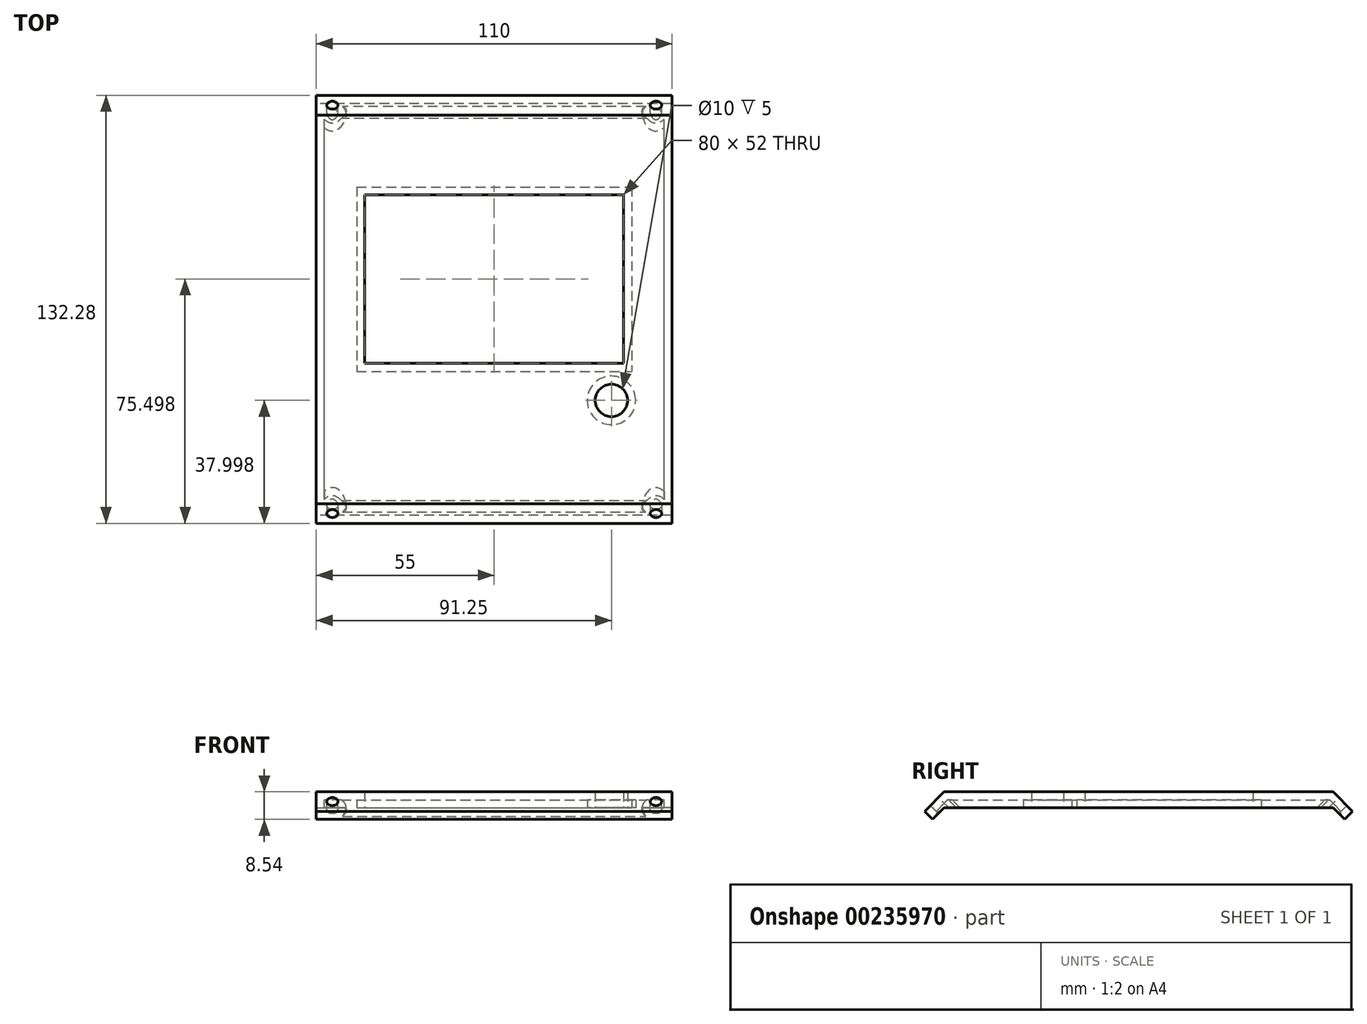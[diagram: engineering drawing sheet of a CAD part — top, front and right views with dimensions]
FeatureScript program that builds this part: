
annotation { "Feature Type Name" : "Feature", "Feature Type Description" : "" }
export const myFeature = defineFeature(function(context is Context, id is Id, definition is map)
    precondition{}
    {
        {
            var Q0;
            Q0=qCreatedBy(makeId("Top.planeOp"),FACE);
            var sketch = newSketch(context, id + "F0", { "sketchPlane" : qUnion([Q0])});
            skLineSegment(sketch, "E0", {"start": v(0, 0) * mm, "end": v(0, 120.2) * mm});
            skLineSegment(sketch, "E1.0", {"start": v(110, 0) * mm, "end": v(110, 120.2) * mm});
            skLineSegment(sketch, "E2", {"start": v(110, 120.2) * mm, "end": v(0, 120.2) * mm});
            skLineSegment(sketch, "E3", {"start": v(0, 0) * mm, "end": v(110, 0) * mm});
            skLineSegment(sketch, "E4.0", {"start": v(15, 95.46) * mm, "end": v(95, 95.46) * mm});
            skLineSegment(sketch, "E5.0", {"start": v(15, 95.46) * mm, "end": v(15, 43.46) * mm});
            skLineSegment(sketch, "E6.0", {"start": v(15, 43.46) * mm, "end": v(95, 43.46) * mm});
            skLineSegment(sketch, "E7.0", {"start": v(95, 95.46) * mm, "end": v(95, 43.46) * mm});
            skCircle(sketch, "E8.0", {"center": v(91.25, 31.96) * mm, "radius": 5 * mm});
            skSolve(sketch);
        }
        {
            var Q0;
            Q0 = qSketchRegion(id + "F0", true);
            extrude(context, id + "F1", {"entities" : qUnion([Q0]), "depth" : 5 * mm});
        }
        {
            var Q0;
            Q0=makeQuery(id+"F1.opExtrude","SWEPT_FACE",FACE,{"disambiguationData":[OSD([sQuery(id+"F0.wireOp",EDGE,"E0")])]});
            var sketch = newSketch(context, id + "F2", { "sketchPlane" : qUnion([Q0])});
            skLineSegment(sketch, "E9", {"start": v(0, 0) * mm, "end": v(3.54, -3.54) * mm});
            skLineSegment(sketch, "E10", {"start": v(3.54, -3.54) * mm, "end": v(6.04, -1.04) * mm});
            skLineSegment(sketch, "E11", {"start": v(6.04, -1.04) * mm, "end": v(0, 5) * mm});
            skLineSegment(sketch, "E12", {"start": v(-120.2, 0) * mm, "end": v(-123.74, -3.54) * mm});
            skLineSegment(sketch, "E13", {"start": v(-123.74, -3.54) * mm, "end": v(-126.24, -1.04) * mm});
            skLineSegment(sketch, "E14", {"start": v(-126.24, -1.04) * mm, "end": v(-120.2, 5) * mm});
            skLineSegment(sketch, "E15", {"start": v(-120.2, 0) * mm, "end": v(-120.2, 5) * mm});
            skLineSegment(sketch, "E16", {"start": v(0, 0) * mm, "end": v(0, 5) * mm});
            skSolve(sketch);
        }
        {
            var Q0;
            Q0 = qSketchRegion(id + "F2", true);
            var Q1;
            Q1=makeQuery(id+"F1.opExtrude","SWEPT_FACE",FACE,{"disambiguationData":[OSD([sQuery(id+"F0.wireOp",EDGE,"E1.0")])]});
            extrude(context, id + "F3", {"entities" : qUnion([Q0]), "operationType" : NewBodyOperationType.ADD, "endBound" : BoundingType.UP_TO_SURFACE, "oppositeDirection" : true, "endBoundEntityFace" : qUnion([Q1]), "depth" : 25 * mm});
        }
        {
            var Q0;
            Q0=makeQuery(id+"F3.opExtrude","SWEPT_FACE",FACE,{"disambiguationData":[OSD([sQuery(id+"F2.wireOp",EDGE,"E14")])]});
            var sketch = newSketch(context, id + "F4", { "sketchPlane" : qUnion([Q0])});
            skCircle(sketch, "E17", {"center": v(-5, -85.73) * mm, "radius": 1.75 * mm});
            skPoint(sketch, "E17.centerSnap0", {"position": v(0, -85.73) * mm});
            skCircle(sketch, "E18", {"center": v(-105, -85.73) * mm, "radius": 1.75 * mm});
            skSolve(sketch);
        }
        {
            var Q0;
            Q0 = qSketchRegion(id + "F4", true);
            extrude(context, id + "F5", {"entities" : qUnion([Q0]), "operationType" : NewBodyOperationType.REMOVE, "endBound" : BoundingType.THROUGH_ALL, "oppositeDirection" : true, "depth" : 25 * mm});
        }
        {
            var Q0;
            Q0=makeQuery(id+"F3.opExtrude","SWEPT_FACE",FACE,{"disambiguationData":[OSD([sQuery(id+"F2.wireOp",EDGE,"E11")])]});
            var sketch = newSketch(context, id + "F6", { "sketchPlane" : qUnion([Q0])});
            skCircle(sketch, "E19", {"center": v(105, -0.73) * mm, "radius": 1.75 * mm});
            skPoint(sketch, "E19.centerSnap0", {"position": v(110, -0.73) * mm});
            skCircle(sketch, "E20", {"center": v(5, -0.73) * mm, "radius": 1.75 * mm});
            skSolve(sketch);
        }
        {
            var Q0;
            Q0 = qSketchRegion(id + "F6", true);
            extrude(context, id + "F7", {"entities" : qUnion([Q0]), "operationType" : NewBodyOperationType.REMOVE, "endBound" : BoundingType.THROUGH_ALL, "oppositeDirection" : true, "depth" : 25 * mm});
        }
        {
            var Q0;
            Q0=makeQuery(id+"F1.opExtrude","CAP_FACE",FACE,{"disambiguationData":[OSD([sQuery(id+"F0.wireOp",EDGE,"E0"),sQuery(id+"F0.wireOp",EDGE,"E2"),sQuery(id+"F0.wireOp",EDGE,"E1.0"),sQuery(id+"F0.wireOp",EDGE,"E3"),sQuery(id+"F0.wireOp",EDGE,"E4.0"),sQuery(id+"F0.wireOp",EDGE,"E5.0"),sQuery(id+"F0.wireOp",EDGE,"E6.0"),sQuery(id+"F0.wireOp",EDGE,"E7.0"),sQuery(id+"F0.wireOp",EDGE,"E8.0")])],"isStart":true});
            shell(context, id + "F8", {"entities" : qUnion([Q0]), "thickness" : 2.5 * mm});
        }
        {
            var Q0;
            Q0=makeQuery(id+"F8.opShell","OFFSET_EDGE",EDGE,{"disambiguationData":[OSD([sQuery(id+"F0.wireOp",EDGE,"E0"),sQuery(id+"F0.wireOp",EDGE,"E2"),sQuery(id+"F2.wireOp",EDGE,"E12"),sQuery(id+"F2.wireOp",EDGE,"E15")]),OD(1.0)]});
            var Q1;
            Q1=makeQuery(id+"F8.opShell","OFFSET_EDGE",EDGE,{"disambiguationData":[OSD([sQuery(id+"F0.wireOp",EDGE,"E0"),sQuery(id+"F0.wireOp",EDGE,"E3"),sQuery(id+"F2.wireOp",EDGE,"E9"),sQuery(id+"F2.wireOp",EDGE,"E16")]),OD(1.0)]});
            chamfer(context, id + "F9", {"entities" : qUnion([Q0, Q1]), "width" : 1.5 * mm, "tangentPropagation" : true});
        }
        {
            var Q0;
            Q0=makeQuery(id+"F9.opChamfer","BLEND_EDGE",EDGE,{"blendedFrom":[makeQuery(id+"F8.opShell","OFFSET_EDGE",EDGE,{"disambiguationData":[OSD([sQuery(id+"F0.wireOp",EDGE,"E0"),sQuery(id+"F0.wireOp",EDGE,"E3"),sQuery(id+"F2.wireOp",EDGE,"E9"),sQuery(id+"F2.wireOp",EDGE,"E16")]),OD(1.0)]}),makeQuery(id+"F8.opShell","OFFSET_FACE",FACE,{"disambiguationData":[OSD([sQuery(id+"F2.wireOp",EDGE,"E11")])]})],"blendedInto":[makeQuery(id+"F8.opShell","OFFSET_FACE",FACE,{"disambiguationData":[OSD([sQuery(id+"F2.wireOp",EDGE,"E11")])]})]});
            var Q1;
            Q1=makeQuery(id+"F9.opChamfer","BLEND_EDGE",EDGE,{"blendedFrom":[makeQuery(id+"F8.opShell","OFFSET_EDGE",EDGE,{"disambiguationData":[OSD([sQuery(id+"F0.wireOp",EDGE,"E0"),sQuery(id+"F0.wireOp",EDGE,"E2"),sQuery(id+"F2.wireOp",EDGE,"E12"),sQuery(id+"F2.wireOp",EDGE,"E15")]),OD(1.0)]}),makeQuery(id+"F8.opShell","OFFSET_FACE",FACE,{"disambiguationData":[OSD([sQuery(id+"F2.wireOp",EDGE,"E14")])]})],"blendedInto":[makeQuery(id+"F8.opShell","OFFSET_FACE",FACE,{"disambiguationData":[OSD([sQuery(id+"F2.wireOp",EDGE,"E14")])]})]});
            fillet(context, id + "F10", {"entities" : qUnion([Q0, Q1]), "radius" : 5 * mm, "tangentPropagation" : true, "allowEdgeOverflow" : false});
        }
    });
